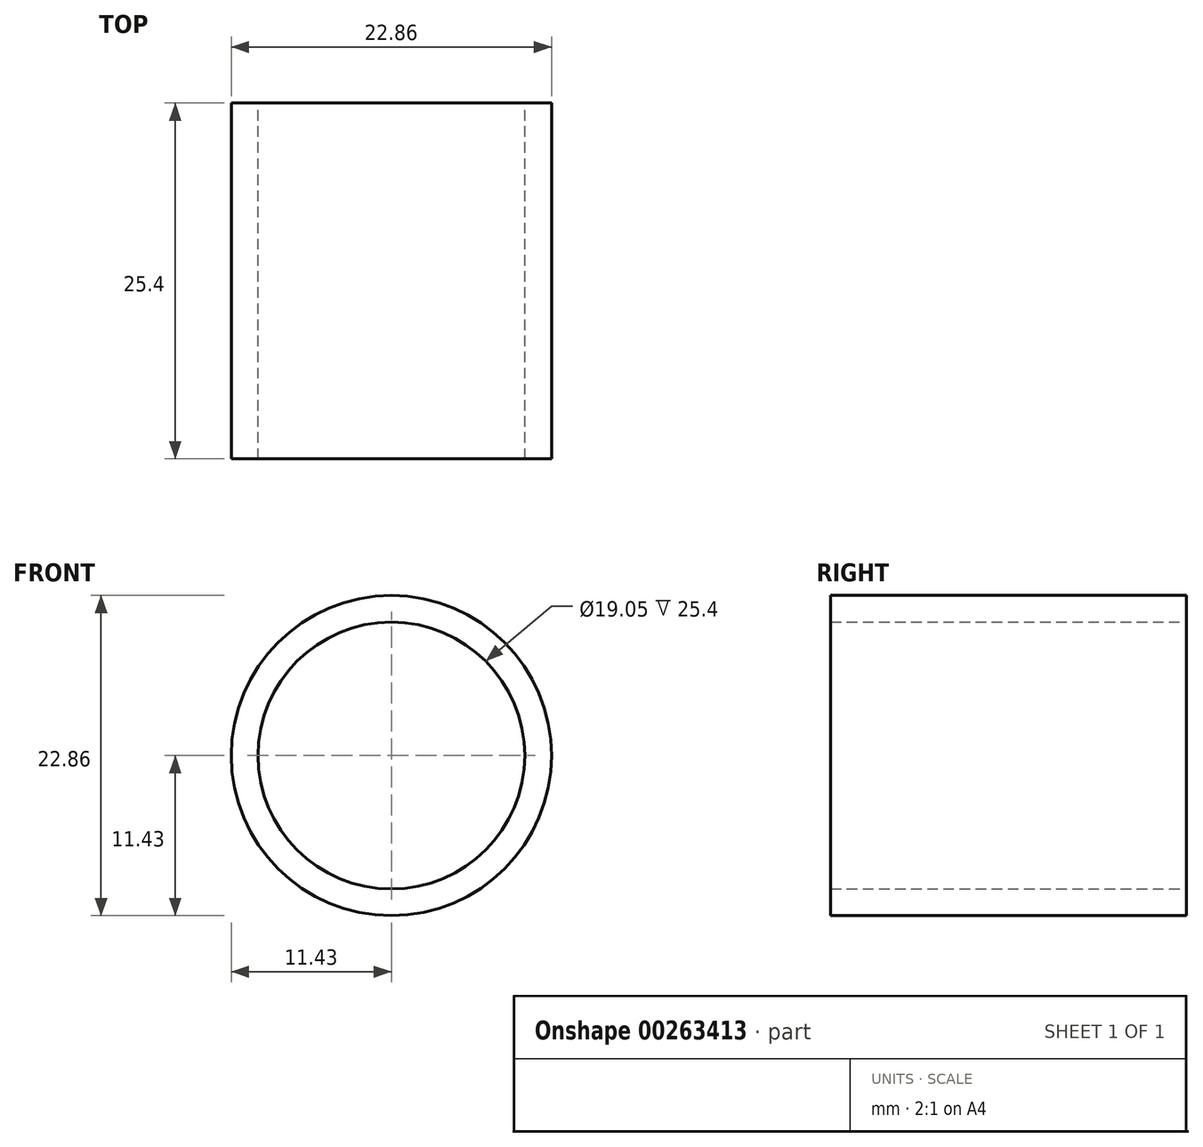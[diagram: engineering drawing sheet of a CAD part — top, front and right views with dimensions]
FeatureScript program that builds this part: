
annotation { "Feature Type Name" : "Feature", "Feature Type Description" : "" }
export const myFeature = defineFeature(function(context is Context, id is Id, definition is map)
    precondition{}
    {
        {
            var Q0;
            Q0=qCreatedBy(makeId("Front.planeOp"),FACE);
            var sketch = newSketch(context, id + "F0", { "sketchPlane" : qUnion([Q0])});
            skCircle(sketch, "E0", {"center": v(0, 0) * mm, "radius": 11.43 * mm});
            skCircle(sketch, "E1", {"center": v(0, 0) * mm, "radius": 9.53 * mm});
            skSolve(sketch);
        }
        {
            var Q0;
            Q0 = qSketchRegion(id + "F0", true);
            extrude(context, id + "F1", {"entities" : qUnion([Q0]), "depth" : 25.4 * mm});
        }
        {
            var Q0;
            Q0 = qSketchRegion(id + "F0", true);
            extrude(context, id + "F2", {"entities" : qUnion([Q0]), "operationType" : NewBodyOperationType.REMOVE, "oppositeDirection" : true, "depth" : 25.4 * mm});
        }
    });
